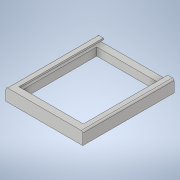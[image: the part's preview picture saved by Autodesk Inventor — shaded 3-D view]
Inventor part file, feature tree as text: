
AUTODESK INVENTOR PART (.ipt)
format: ipt  version: 2020 (Build 240168000, 168)  size: 242,688 bytes
history: native  units: mm
features: extrude x6, sketch x5, fillet x2
ambient origin geometry x8: Origin, YZ Plane, XZ Plane, XY Plane, X Axis, Y Axis, Z Axis, Center Point
bodies: Solid1 (feature_tree)
feature tree (13):
  extrude  "Base"  Depth=170.0mm
  extrude  "Extrusion2"  Depth=120.0mm
  extrude  "Extrusion3"  Depth=23.0mm TaperAngle=0.0deg
  extrude  "Extrusion4"  Depth=3.65mm
  fillet  "Fillet1"  Radius=5.2mm
  extrude  "Extrusion5"  Depth=12.0mm TaperAngle=0.0deg
  fillet  "Fillet2"  Radius=12.0mm
  extrude  "Extrusion6"  Depth=15.0mm
  sketch  "Sketch1"  dims[d0=143.0mm d1=170.0mm]
  sketch  "Sketch2"  dims[d2=23.0mm d3=0.0mm d4=120.0mm]
  sketch  "Sketch4"  dims[d5=145.0mm d6=23.0mm d7=0.0mm]
  sketch  "Sketch5"  dims[d8=3.65mm d9=3.65mm d10=5.2mm]
  sketch  "Sketch6"  dims[d11=12.5mm d12=12.0mm d13=0.0mm d14=12.0mm d15=15.0mm d16=12.0mm d17=14.3mm d18=12.0mm d19=12.0mm d20=14.3mm d21=12.0mm d22=12.0mm d23=15.0mm d24=12.0mm d25=12.0mm d26=7.0mm d27=0.0mm d28=1.25mm d29=133.0mm d30=5.25mm d31=14.8mm d32=165.0mm d33=0.0mm d34=3.0mm d35=120.0mm d36=12.5mm d37=0.0mm d38=5.2mm d39=151.0mm]
